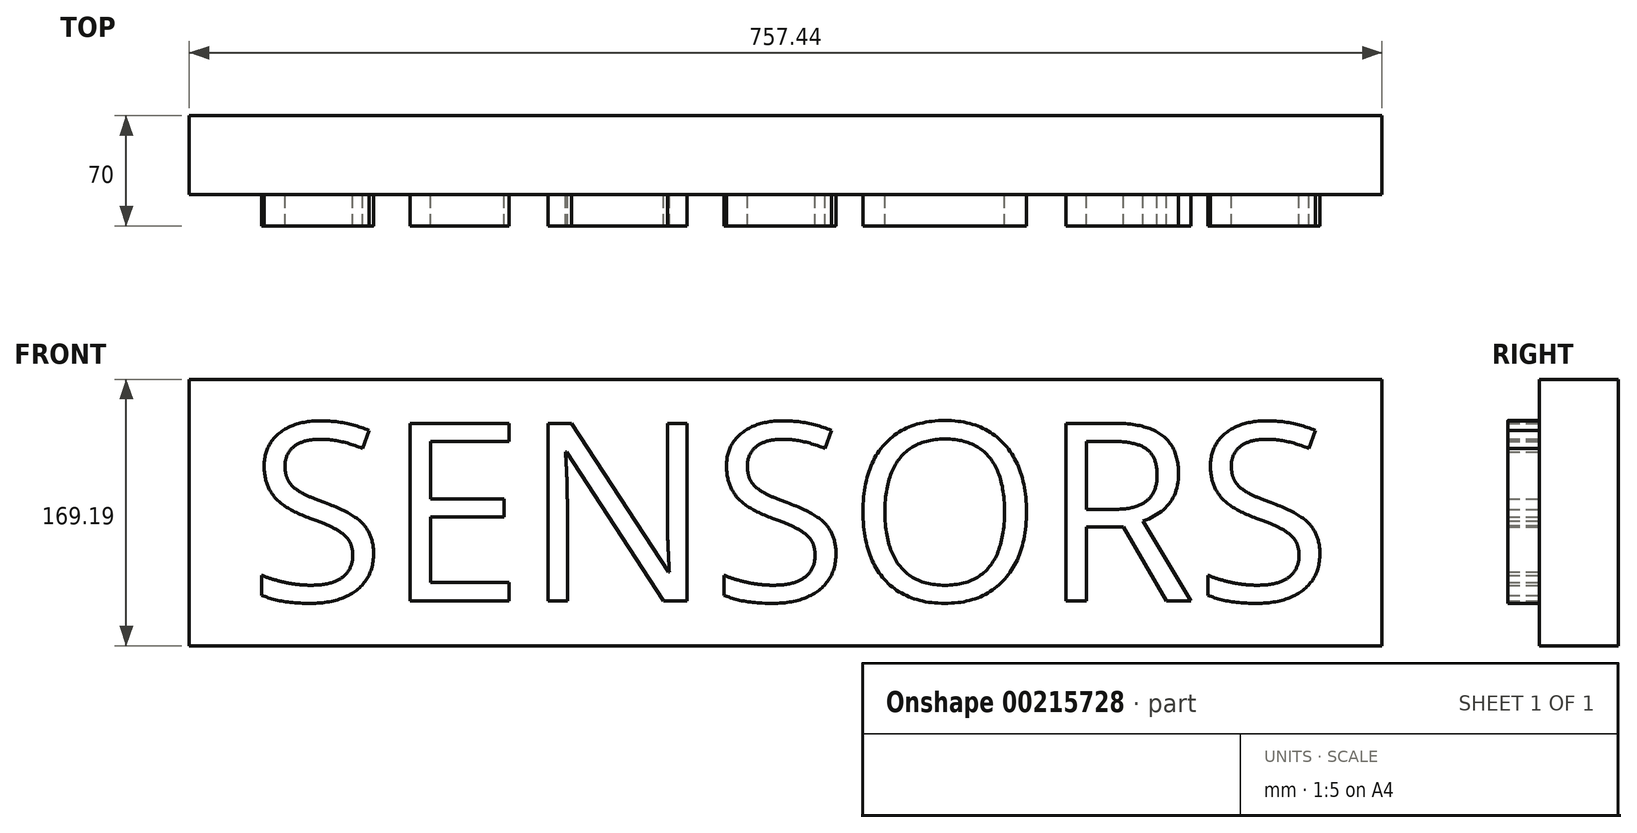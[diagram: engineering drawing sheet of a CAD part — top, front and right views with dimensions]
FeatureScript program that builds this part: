
annotation { "Feature Type Name" : "Feature", "Feature Type Description" : "" }
export const myFeature = defineFeature(function(context is Context, id is Id, definition is map)
    precondition{}
    {
        {
            var Q0;
            Q0=qCreatedBy(makeId("Front.planeOp"),FACE);
            var sketch = newSketch(context, id + "F0", { "sketchPlane" : qUnion([Q0])});
            skLineSegment(sketch, "E0.bottom", {"start": v(0, 0) * mm, "end": v(757.44, 0) * mm});
            skLineSegment(sketch, "E0.top", {"start": v(0, 169.2) * mm, "end": v(757.44, 169.2) * mm});
            skLineSegment(sketch, "E0.left", {"start": v(0, 0) * mm, "end": v(0, 169.2) * mm});
            skLineSegment(sketch, "E0.right", {"start": v(757.44, 0) * mm, "end": v(757.44, 169.2) * mm});
            skSolve(sketch);
        }
        {
            var Q0;
            Q0=qSketchRegion(id+"F0",true);
            extrude(context, id + "F1", {"entities" : qUnion([Q0]), "depth" : 50 * mm});
        }
        {
            var Q0;
            Q0=qCreatedBy(makeId("Front.planeOp"),FACE);
            var sketch = newSketch(context, id + "F2", { "sketchPlane" : qUnion([Q0])});
            skText(sketch, "E1", { "text": "SENSORS", "fontName": "OpenSans-Regular.ttf"});
            const initialGuessF2  = {"E1": [0.03787, 0.02852, 1, 0, 0.11374]};
            skSetInitialGuess(sketch, initialGuessF2);
            skSolve(sketch);
        }
        {
            var Q0;
            Q0 = qSketchRegion(id + "F2", true);
            extrude(context, id + "F3", {"entities" : qUnion([Q0]), "operationType" : NewBodyOperationType.ADD, "depth" : 70 * mm});
        }
    });
